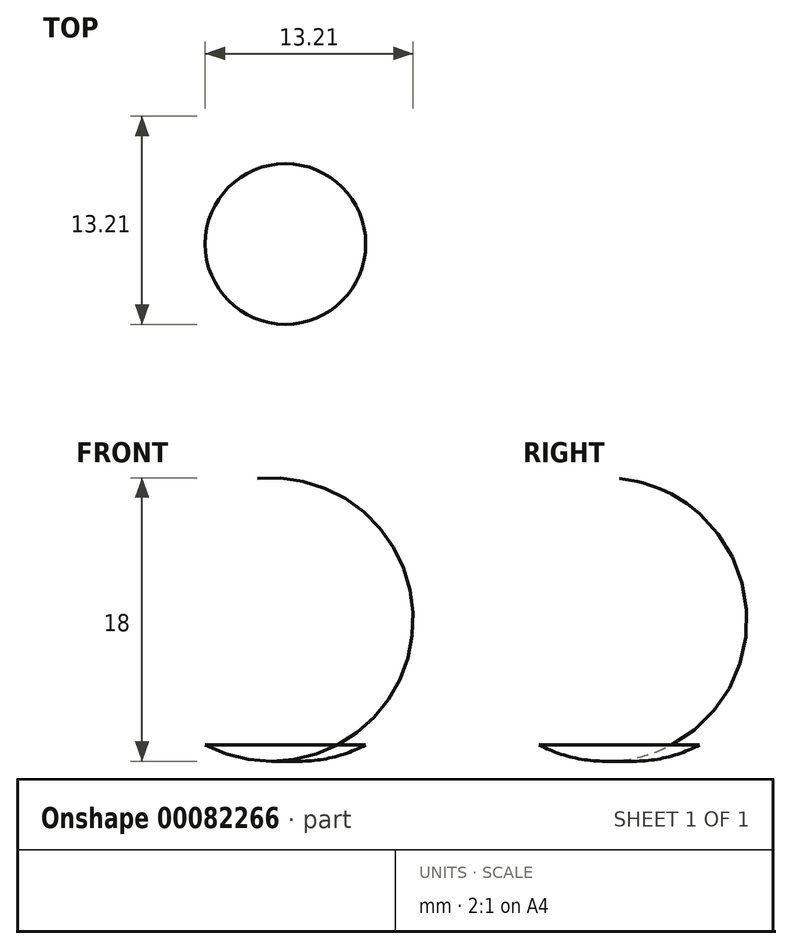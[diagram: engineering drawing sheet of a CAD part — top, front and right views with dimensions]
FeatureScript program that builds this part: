
annotation { "Feature Type Name" : "Feature", "Feature Type Description" : "" }
export const myFeature = defineFeature(function(context is Context, id is Id, definition is map)
    precondition{}
    {
        {
            var Q0;
            Q0=qCreatedBy(makeId("Front.planeOp"),FACE);
            var sketch = newSketch(context, id + "F0", { "sketchPlane" : qUnion([Q0])});
            skLineSegment(sketch, "E0", {"start": v(0, 0) * mm, "end": v(0, 1) * mm});
            skLineSegment(sketch, "E1", {"start": v(0, 1) * mm, "end": v(5.1, 1) * mm});
            skArc(sketch, "E2", {"start": v(0, 0) * mm, "mid": v(2.62, 0.12) * mm, "end": v(5.1, 1) * mm});
            skSolve(sketch);
        }
        {
            var Q0;
            Q0=makeQuery(id+"F0.imprint","IMPRINT",FACE,{"disambiguationData":[TD([[makeQuery(id+"F0.imprint","IMPRINT",EDGE,{"derivedFrom":sQuery(id+"F0.wireOp",EDGE,"E0")}),-1.0]])]});
            var Q1;
            Q1=sQuery(id+"F0.wireOp",EDGE,"E0");
            revolve(context, id + "F1", {"entities" : qUnion([Q0]), "axis" : qUnion([Q1]), "revolveType" : RevolveType.FULL});
        }
    });
